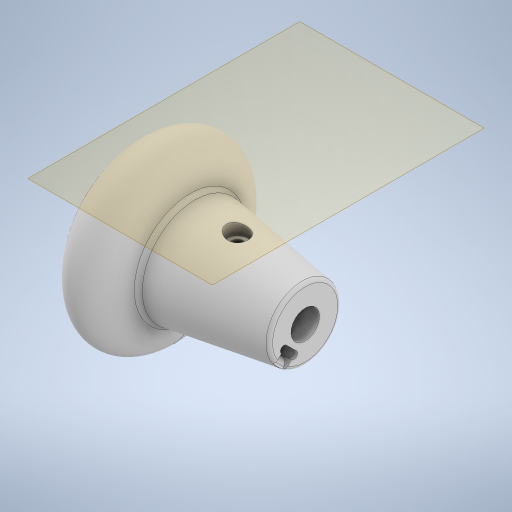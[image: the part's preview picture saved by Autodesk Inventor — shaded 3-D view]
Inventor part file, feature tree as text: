
AUTODESK INVENTOR PART (.ipt)
format: ipt  version: 2024.2 (Build 282272000, 272)  size: 551,936 bytes
history: native  units: mm
features: sketch x19, extrude x12, plane x3, revolve x2, other x2, loft x1, fillet x1, projected_geometry x1
ambient origin geometry x8: Origin, YZ Plane, XZ Plane, XY Plane, X Axis, Y Axis, Z Axis, Center Point
bodies: Solid1 (feature_tree)
feature tree (41):
  revolve  "Revolution1"  [1 undecoded]
  extrude  "Extrusion1"  Depth=2.0mm
  extrude  "Extrusion2"  Depth=7.0mm
  plane  "Work Plane2"
  sketch  "Sketch4"  dims[d24=33.0mm d25=0.0mm d26=1.0mm d27=0.0mm]
  extrude  "Extrusion3"  Depth=1.0mm TaperAngle=0.0deg
  revolve  "Revolution2"  [1 undecoded]
  sketch  "Sketch9"  dims[d55=30.591983mm d56=11.079807mm]
  sketch  "Sketch11"  dims[d58=41.0mm d59=11.079948mm]
  sketch  "Sketch12"  dims[d60=2.0mm d61=14.6mm]
  sketch  "Sketch13"  dims[d62=13.0mm d63=34.0mm d65=22.0mm]
  extrude  "Extrusion7"  TaperAngle=90.0deg  [1 undecoded]
  sketch  "Sketch17"  dims[d69=2.0mm d70=2.0mm]
  sketch  "Sketch18"  dims[d71=4.0mm d72=15.0mm d73=0.0mm]
  extrude  "Extrusion8"  Depth=11.079807mm
  extrude  "Extrusion9"  Depth=11.079948mm
  loft  "Loft2"
  extrude  "Extrusion10"  Depth=34.0mm
  fillet  "Fillet1"  Radius=22.0mm
  extrude  "Extrusion11"  Depth=3.0mm
  extrude  "Extrusion12"  Depth=2.0mm
  plane  "Work Plane3"
  extrude  "Extrusion13"  Depth=15.0mm TaperAngle=0.0deg
  extrude  "Extrusion14"  Depth=2.5mm
  extrude  "Extrusion15"  Depth=2.0mm
  sketch  "Sketch1"  dims[d0=10.0mm d11=1.0mm]
  sketch  "Sketch2"  dims[d19=25.0mm d20=2.0mm]
  sketch  "Sketch3"  dims[d22=360.0deg d23=7.0mm]
  plane  "Work Plane1"
  sketch  "Sketch5"  dims[d28=-3.5mm d29=1.0mm d30=0.0mm]
  sketch  "Sketch6"  dims[d34=16.739289mm d35=90.0deg]
  sketch  "Sketch14"  dims[d67=3.0mm d68=1.0mm]
  other  "Edges3"
  other  "Edges4"
  sketch  "Sketch19"  dims[d74=24.0mm d76=2.5mm]
  projected_geometry  "Projected Loop1"
  sketch  "Sketch20"  dims[d77=4.0mm d78=2.0mm]
  sketch  "Sketch21"  dims[d79=1.0mm d80=0.0mm]
  sketch  "Sketch22"  dims[d81=1.0mm d82=0.0mm]
  sketch  "Sketch23"  dims[d83=0.0mm d84=90.0deg]
  sketch  "Sketch24"  dims[d85=0.0mm d86=90.0deg d87=3.0mm d88=0.0mm d89=2.0mm d90=2.0mm d91=2.5mm d92=2.5mm d93=2.5mm d94=1.5mm d95=0.0mm d96=8.0mm d97=10.0mm d98=0.0mm d99=3.0mm d100=22.0mm d101=0.0mm d103=19.0mm d104=3.5mm d105=20.0mm d106=0.0mm d107=6.0mm d108=15.0mm d109=0.0mm]
note: 3 required parameter values undecoded (feature->parameter linkage not recoverable at this tier; creation-order binding heuristic only, values carry confidence <= 0.55)